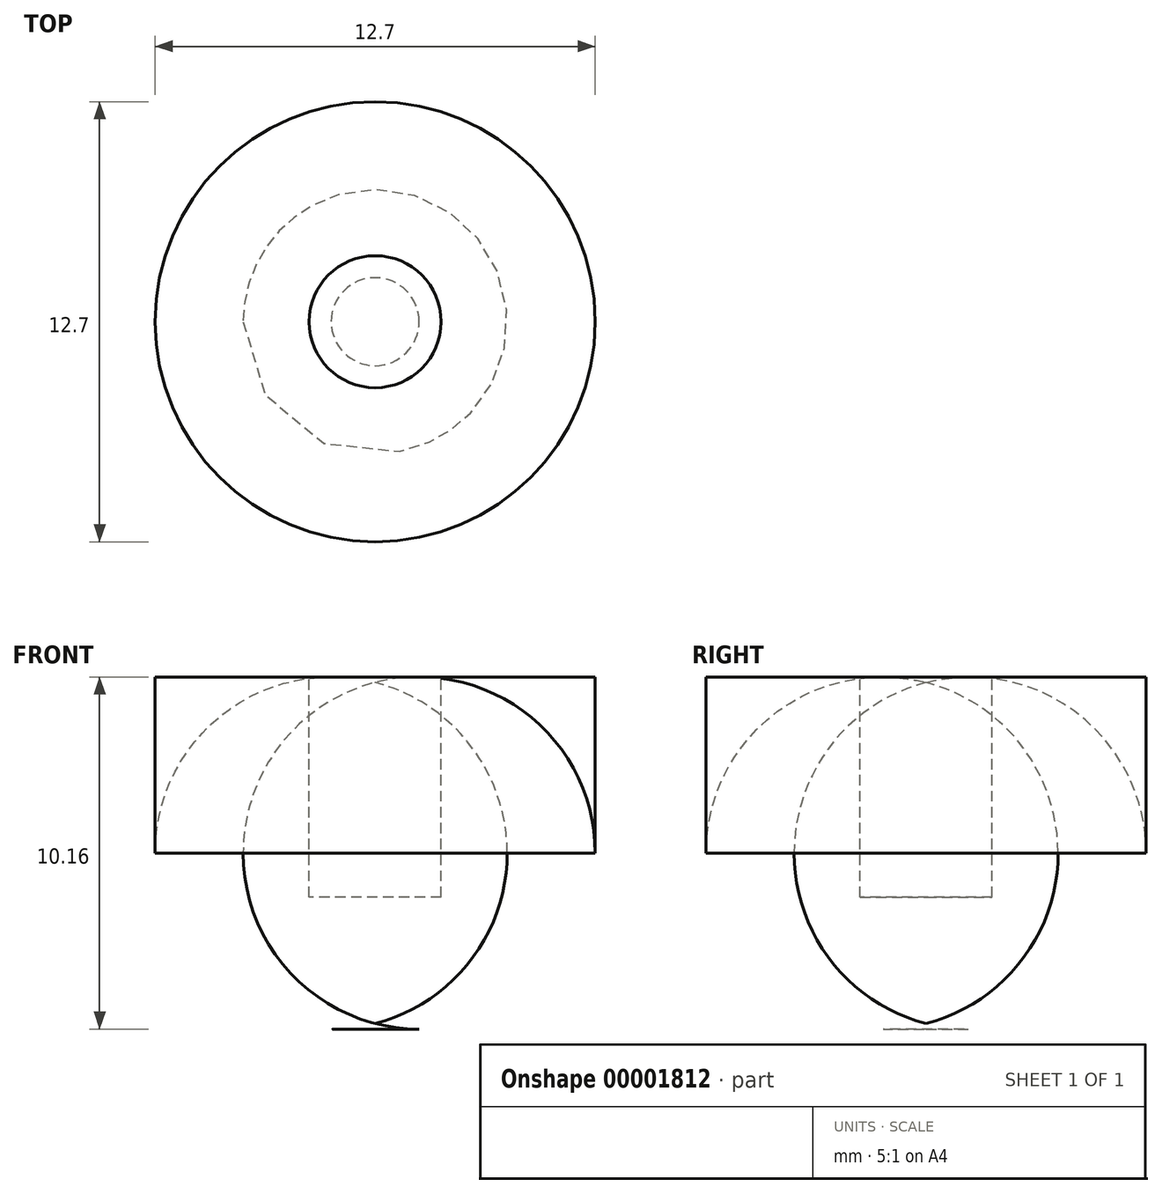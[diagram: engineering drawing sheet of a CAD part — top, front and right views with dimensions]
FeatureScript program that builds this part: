
annotation { "Feature Type Name" : "Feature", "Feature Type Description" : "" }
export const myFeature = defineFeature(function(context is Context, id is Id, definition is map)
    precondition{}
    {
        {
            var Q0;
            Q0=qCreatedBy(makeId("Top.planeOp"),FACE);
            var sketch = newSketch(context, id + "F0", { "sketchPlane" : qUnion([Q0])});
            skCircle(sketch, "E0", {"center": v(0, 0) * mm, "radius": 6.35 * mm});
            skSolve(sketch);
        }
        {
            var Q0;
            Q0=makeQuery(id+"F0.imprint","IMPRINT",FACE,{"disambiguationData":[TD([[makeQuery(id+"F0.imprint","IMPRINT",EDGE,{"derivedFrom":sQuery(id+"F0.wireOp",EDGE,"E0")}),1.0]])]});
            extrude(context, id + "F1", {"entities" : qUnion([Q0]), "depth" : 10.16 * mm});
        }
        {
            var Q0;
            Q0=makeQuery(id+"F1.opExtrude","CAP_FACE",FACE,{"disambiguationData":[OSD([sQuery(id+"F0.wireOp",EDGE,"E0")])],"isStart":false});
            var sketch = newSketch(context, id + "F2", { "sketchPlane" : qUnion([Q0])});
            skCircle(sketch, "E1", {"center": v(0, 0) * mm, "radius": 1.9 * mm});
            skSolve(sketch);
        }
        {
            var Q0;
            Q0=makeQuery(id+"F2.imprint","IMPRINT",FACE,{"disambiguationData":[TD([[makeQuery(id+"F2.imprint","IMPRINT",EDGE,{"derivedFrom":sQuery(id+"F2.wireOp",EDGE,"E1")}),1.0]])]});
            extrude(context, id + "F3", {"entities" : qUnion([Q0]), "operationType" : NewBodyOperationType.REMOVE, "oppositeDirection" : true, "depth" : 6.35 * mm});
        }
        {
            var Q0;
            Q0=makeQuery(id+"F1.opExtrude","CAP_EDGE",EDGE,{"disambiguationData":[OSD([sQuery(id+"F0.wireOp",EDGE,"E0")])],"isStart":true});
            fillet(context, id + "F4", {"entities" : qUnion([Q0]), "radius" : 5.08 * mm, "tangentPropagation" : true, "allowEdgeOverflow" : false});
        }
    });
